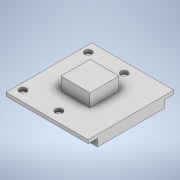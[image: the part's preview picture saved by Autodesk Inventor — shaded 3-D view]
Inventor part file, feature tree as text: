
AUTODESK INVENTOR PART (.ipt)
format: ipt  version: 2020 (Build 240168000, 168)  size: 132,608 bytes
history: native  units: in
note: dims shown in document units (in); Inventor stores cm internally (conversion verified against a paired STEP export)
features: extrude x3, sketch x3
ambient origin geometry x8: Origin, YZ Plane, XZ Plane, XY Plane, X Axis, Y Axis, Z Axis, Center Point
bodies: Solid1 (feature_tree)
feature tree (6):
  extrude  "Extrusion1"  Depth=0.9395in
  extrude  "Extrusion2"  Depth=0.0758in
  extrude  "Extrusion3"  Depth=0.04in TaperAngle=0.0deg
  sketch  "Sketch1"  dims[d0=0.9815in d1=0.9395in]
  sketch  "Sketch2"  dims[d2=0.0815in d3=0.0758in]
  sketch  "Sketch3"  dims[d5=0.206in d6=0.04in d7=0.0in d8=0.3315in d9=0.3315in d10=0.15in d11=0.0in d12=0.21in d13=0.768in d14=0.086in d15=0.0in d16=0.7475in]
